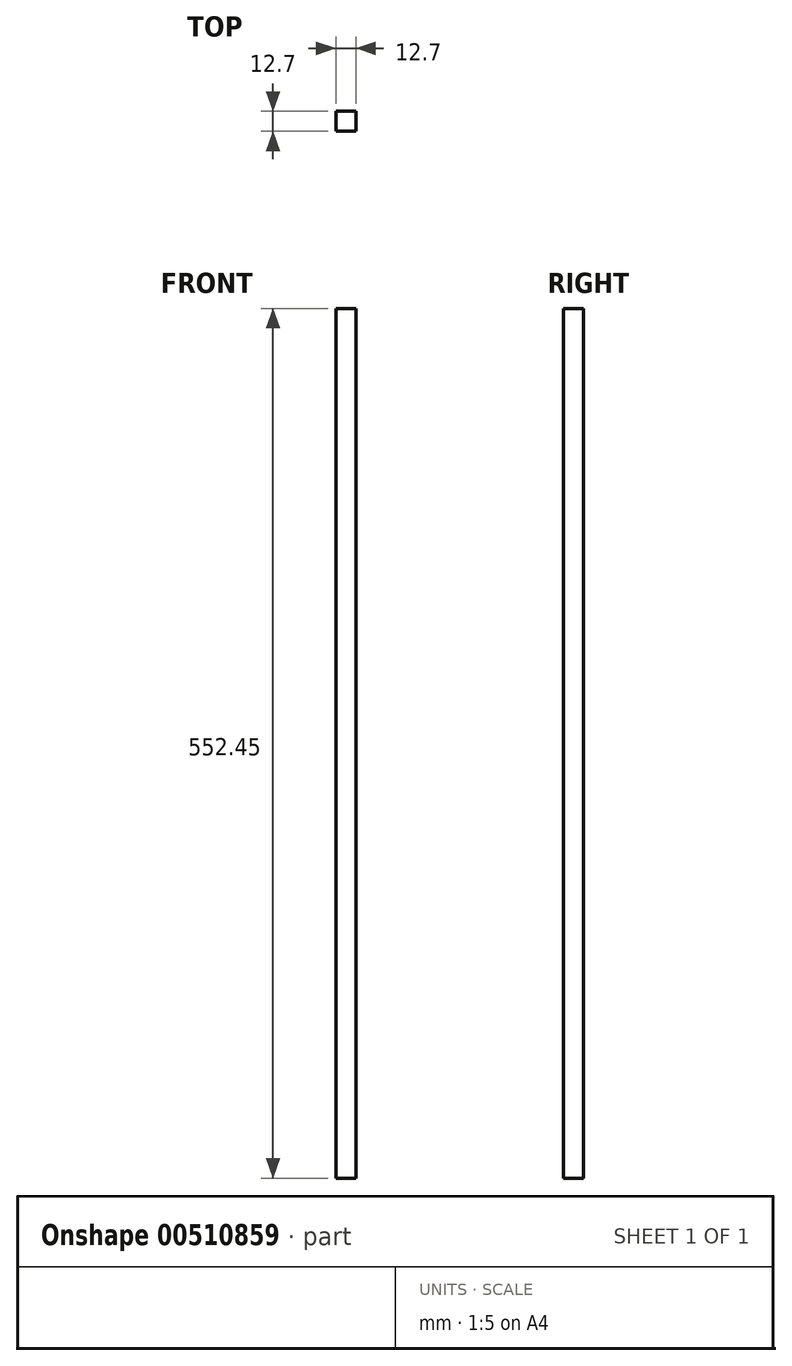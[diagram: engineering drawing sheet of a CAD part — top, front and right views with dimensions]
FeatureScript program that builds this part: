
annotation { "Feature Type Name" : "Feature", "Feature Type Description" : "" }
export const myFeature = defineFeature(function(context is Context, id is Id, definition is map)
    precondition{}
    {
        {
            var Q0;
            Q0=qCreatedBy(makeId("Top.planeOp"),FACE);
            var sketch = newSketch(context, id + "F0", { "sketchPlane" : qUnion([Q0])});
            skLineSegment(sketch, "E0.bottom", {"start": v(-50.2, -8.24) * mm, "end": v(-37.5, -8.24) * mm});
            skLineSegment(sketch, "E0.top", {"start": v(-50.2, -20.94) * mm, "end": v(-37.5, -20.94) * mm});
            skLineSegment(sketch, "E0.left", {"start": v(-50.2, -8.24) * mm, "end": v(-50.2, -20.94) * mm});
            skLineSegment(sketch, "E0.right", {"start": v(-37.5, -8.24) * mm, "end": v(-37.5, -20.94) * mm});
            skSolve(sketch);
        }
        {
            var Q0;
            Q0=makeQuery(id+"F0.imprint","IMPRINT",FACE,{"disambiguationData":[TD([[makeQuery(id+"F0.imprint","IMPRINT",EDGE,{"derivedFrom":sQuery(id+"F0.wireOp",EDGE,"E0.bottom")}),-1.0]])]});
            extrude(context, id + "F1", {"entities" : qUnion([Q0]), "depth" : 552.45 * mm, "offsetDistance" : 25.4 * mm});
        }
    });
